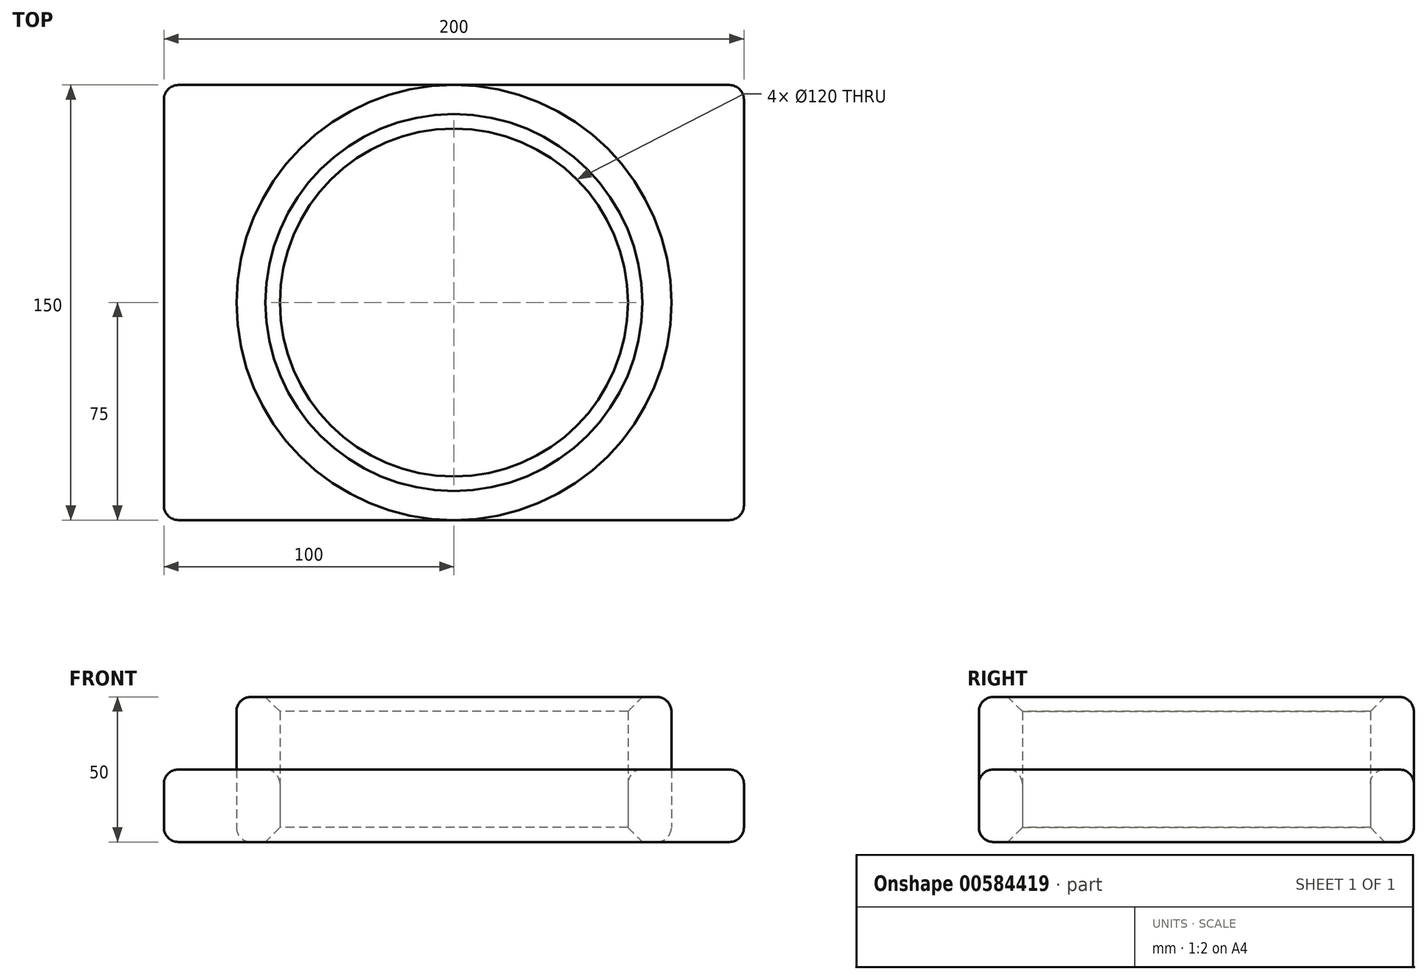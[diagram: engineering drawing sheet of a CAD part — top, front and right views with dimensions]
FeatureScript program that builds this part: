
annotation { "Feature Type Name" : "Feature", "Feature Type Description" : "" }
export const myFeature = defineFeature(function(context is Context, id is Id, definition is map)
    precondition{}
    {
        {
            var Q0;
            Q0=qCreatedBy(makeId("Top.planeOp"),FACE);
            var sketch = newSketch(context, id + "F0", { "sketchPlane" : qUnion([Q0])});
            skCircle(sketch, "E0", {"center": v(0, 0) * mm, "radius": 75 * mm});
            skLineSegment(sketch, "E1.bottom", {"start": v(-100, 75) * mm, "end": v(100, 75) * mm});
            skLineSegment(sketch, "E1.top", {"start": v(-100, -75) * mm, "end": v(100, -75) * mm});
            skLineSegment(sketch, "E1.left", {"start": v(-100, 75) * mm, "end": v(-100, -75) * mm});
            skLineSegment(sketch, "E1.right", {"start": v(100, 75) * mm, "end": v(100, -75) * mm});
            skLineSegment(sketch, "E2", {"start": v(-100, 75) * mm, "end": v(100, -75) * mm, "construction": true});
            skCircle(sketch, "E3.0", {"center": v(0, 0) * mm, "radius": 60 * mm});
            skSolve(sketch);
        }
        {
            var Q0;
            {var subQ0=sQuery(id+"F0.wireOp",EDGE,"E0");var subQ1=makeQuery(id+"F0.imprint","INTERSECT",VERTEX,{"derivedFrom":[subQ0,sQuery(id+"F0.wireOp",EDGE,"E1.bottom")]});Q0=makeQuery(id+"F0.imprint","IMPRINT",FACE,{"disambiguationData":[TD([[makeQuery(id+"F0.imprint","IMPRINT",EDGE,{"disambiguationData":[TD([[subQ1,-1.0]])],"derivedFrom":subQ0}),1.0]])]});}
            extrude(context, id + "F1", {"entities" : qUnion([Q0]), "depth" : 50 * mm, "offsetDistance" : 25 * mm});
        }
        {
            var Q0;
            Q0 = qSketchRegion(id + "F0", true);
            extrude(context, id + "F2", {"entities" : qUnion([Q0]), "depth" : 25 * mm, "offsetDistance" : 25 * mm});
        }
        {
            var Q0;
            Q0=makeQuery(id+"F1.opExtrude","SWEPT_FACE",FACE,{"disambiguationData":[OSD([sQuery(id+"F0.wireOp",EDGE,"E0")])]});
            var Q1;
            Q1=makeQuery(id+"F2.opExtrude","CAP_FACE",FACE,{"disambiguationData":[OSD([sQuery(id+"F0.wireOp",EDGE,"E1.bottom"),sQuery(id+"F0.wireOp",EDGE,"E1.top"),sQuery(id+"F0.wireOp",EDGE,"E1.left"),sQuery(id+"F0.wireOp",EDGE,"E1.right"),sQuery(id+"F0.wireOp",EDGE,"E3.0")])],"isStart":false});
            var Q2;
            Q2=makeQuery(id+"F2.opExtrude","SWEPT_FACE",FACE,{"disambiguationData":[OSD([sQuery(id+"F0.wireOp",EDGE,"E1.left")])]});
            var Q3;
            Q3=makeQuery(id+"F2.opExtrude","SWEPT_FACE",FACE,{"disambiguationData":[OSD([sQuery(id+"F0.wireOp",EDGE,"E1.bottom")])]});
            var Q4;
            Q4=makeQuery(id+"F2.opExtrude","SWEPT_FACE",FACE,{"disambiguationData":[OSD([sQuery(id+"F0.wireOp",EDGE,"E1.top")])]});
            var Q5;
            Q5=makeQuery(id+"F2.opExtrude","SWEPT_FACE",FACE,{"disambiguationData":[OSD([sQuery(id+"F0.wireOp",EDGE,"E1.right")])]});
            fillet(context, id + "F3", {"entities" : qUnion([Q0, Q1, Q2, Q3, Q4, Q5]), "radius" : 5 * mm, "tangentPropagation" : true, "allowEdgeOverflow" : false});
        }
        {
            var Q0;
            Q0=makeQuery(id+"F2.opExtrude","CAP_EDGE",EDGE,{"disambiguationData":[OSD([sQuery(id+"F0.wireOp",EDGE,"E3.0")])],"isStart":true});
            var Q1;
            Q1=makeQuery(id+"F1.opExtrude","SWEPT_FACE",FACE,{"disambiguationData":[OSD([sQuery(id+"F0.wireOp",EDGE,"E3.0")])]});
            chamfer(context, id + "F4", {"entities" : qUnion([Q0, Q1]), "width" : 5 * mm, "tangentPropagation" : true});
        }
    });
